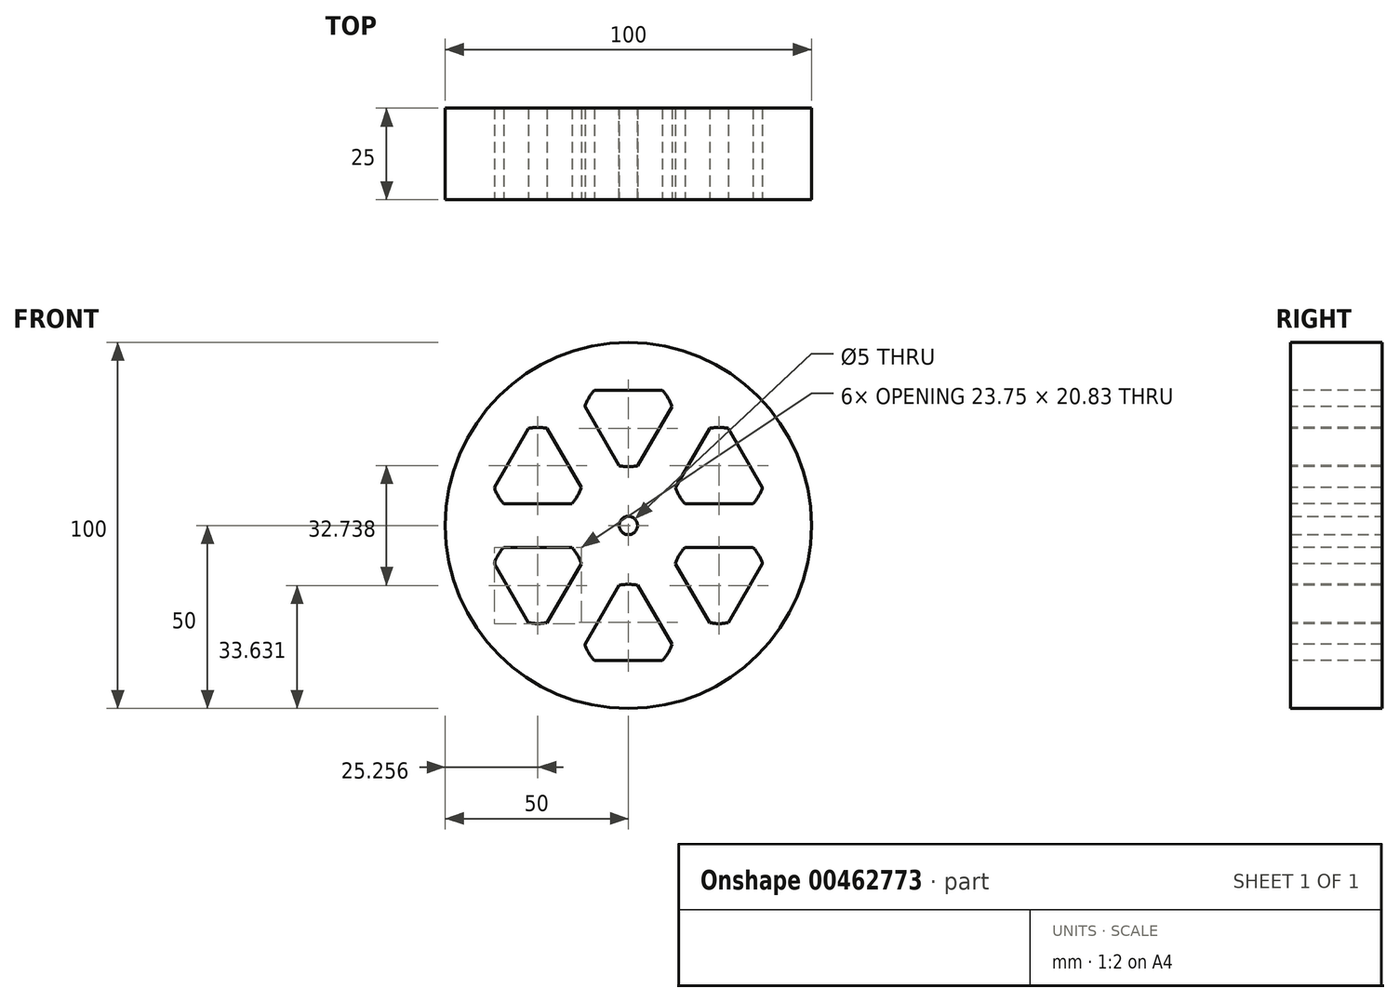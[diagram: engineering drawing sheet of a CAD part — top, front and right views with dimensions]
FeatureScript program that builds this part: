
annotation { "Feature Type Name" : "Feature", "Feature Type Description" : "" }
export const myFeature = defineFeature(function(context is Context, id is Id, definition is map)
    precondition{}
    {
        {
            var Q0;
            Q0=qCreatedBy(makeId("Front.planeOp"),FACE);
            var sketch = newSketch(context, id + "F0", { "sketchPlane" : qUnion([Q0])});
            skCircle(sketch, "E0", {"center": v(0, 0) * mm, "radius": 50 * mm});
            skCircle(sketch, "E1", {"center": v(0, 0) * mm, "radius": 2.5 * mm});
            skSolve(sketch);
        }
        {
            var Q0;
            Q0=qSketchRegion(id+"F0",true);
            extrude(context, id + "F1", {"entities" : qUnion([Q0]), "depth" : 25 * mm});
        }
        {
            var Q0;
            Q0=makeQuery(id+"F1.opExtrude","CAP_FACE",FACE,{"disambiguationData":[OSD([sQuery(id+"F0.wireOp",EDGE,"E0"),sQuery(id+"F0.wireOp",EDGE,"E1")])],"isStart":false});
            var sketch = newSketch(context, id + "F2", { "sketchPlane" : qUnion([Q0])});
            skCircle(sketch, "E2.cCircle", {"center": v(0, 28.57) * mm, "radius": 8.33 * mm, "construction": true});
            skLineSegment(sketch, "E2.0", {"start": v(14.43, 36.9) * mm, "end": v(0, 11.9) * mm});
            skLineSegment(sketch, "E2.1", {"start": v(0, 11.9) * mm, "end": v(-14.43, 36.9) * mm});
            skLineSegment(sketch, "E2.2", {"start": v(-14.43, 36.9) * mm, "end": v(14.43, 36.9) * mm});
            skPoint(sketch, "E2.0.midPoint", {"position": v(7.22, 24.4) * mm});
            skLineSegment(sketch, "E3", {"start": v(0, 0) * mm, "end": v(77.64, 0) * mm, "construction": true});
            skPoint(sketch, "E4.center", {"position": v(0, 0) * mm});
            skLineSegment(sketch, "E5", {"start": v(0, 0) * mm, "end": v(0, 56.69) * mm, "construction": true});
            skCircle(sketch, "E6.cCircle", {"center": v(24.74, 14.29) * mm, "radius": 8.33 * mm, "construction": true});
            skLineSegment(sketch, "E6.0", {"start": v(24.74, 30.95) * mm, "end": v(39.18, 5.95) * mm});
            skLineSegment(sketch, "E6.1", {"start": v(39.18, 5.95) * mm, "end": v(10.3, 5.95) * mm});
            skLineSegment(sketch, "E6.2", {"start": v(10.3, 5.95) * mm, "end": v(24.74, 30.95) * mm});
            skPoint(sketch, "E6.0.midPoint", {"position": v(31.96, 18.45) * mm});
            skLineSegment(sketch, "E7", {"start": v(10.3, 5.95) * mm, "end": v(36.54, 21.1) * mm, "construction": true});
            skLineSegment(sketch, "E8.1.0", {"start": v(-39.18, 5.95) * mm, "end": v(-24.74, 30.95) * mm});
            skLineSegment(sketch, "E8.1.1", {"start": v(-10.3, 5.95) * mm, "end": v(-39.18, 5.95) * mm});
            skLineSegment(sketch, "E8.1.2", {"start": v(-24.74, 30.95) * mm, "end": v(-10.3, 5.95) * mm});
            skLineSegment(sketch, "E8.1.3", {"start": v(-10.3, -5.95) * mm, "end": v(-24.74, -30.95) * mm});
            skLineSegment(sketch, "E8.1.4", {"start": v(-24.74, -30.95) * mm, "end": v(-39.18, -5.95) * mm});
            skLineSegment(sketch, "E8.1.5", {"start": v(-39.18, -5.95) * mm, "end": v(-10.3, -5.95) * mm});
            skLineSegment(sketch, "E8.2.0", {"start": v(14.43, -36.9) * mm, "end": v(-14.43, -36.9) * mm});
            skLineSegment(sketch, "E8.2.1", {"start": v(0, -11.9) * mm, "end": v(14.43, -36.9) * mm});
            skLineSegment(sketch, "E8.2.2", {"start": v(-14.43, -36.9) * mm, "end": v(0, -11.9) * mm});
            skLineSegment(sketch, "E8.2.3", {"start": v(10.3, -5.95) * mm, "end": v(39.18, -5.95) * mm});
            skLineSegment(sketch, "E8.2.4", {"start": v(39.18, -5.95) * mm, "end": v(24.74, -30.95) * mm});
            skLineSegment(sketch, "E8.2.5", {"start": v(24.74, -30.95) * mm, "end": v(10.3, -5.95) * mm});
            skCircle(sketch, "E9", {"center": v(0, 28.57) * mm, "radius": 12.5 * mm});
            skCircle(sketch, "E10", {"center": v(24.74, 14.29) * mm, "radius": 12.5 * mm});
            skCircle(sketch, "E11.1.0", {"center": v(-24.74, -14.29) * mm, "radius": 12.5 * mm});
            skCircle(sketch, "E11.1.1", {"center": v(-24.74, 14.29) * mm, "radius": 12.5 * mm});
            skCircle(sketch, "E11.2.0", {"center": v(24.74, -14.29) * mm, "radius": 12.5 * mm});
            skCircle(sketch, "E11.2.1", {"center": v(0, -28.57) * mm, "radius": 12.5 * mm});
            skSolve(sketch);
        }
        {
            var Q0;
            {var subQ0=sQuery(id+"F2.wireOp",EDGE,"E9");var subQ4=sQuery(id+"F2.wireOp",EDGE,"E2.0");var subQ5=makeQuery(id+"F2.imprint","INTERSECT",VERTEX,{"disambiguationData":[OD(0.0)],"derivedFrom":[subQ4,subQ0]});Q0=makeQuery(id+"F2.imprint","IMPRINT",FACE,{"disambiguationData":[TD([[makeQuery(id+"F2.imprint","IMPRINT",EDGE,{"disambiguationData":[TD([[subQ5,-1.0]])],"derivedFrom":subQ4}),-1.0]])]});}
            var Q1;
            {var subQ0=sQuery(id+"F2.wireOp",EDGE,"E10");var subQ4=sQuery(id+"F2.wireOp",EDGE,"E6.0");var subQ5=makeQuery(id+"F2.imprint","INTERSECT",VERTEX,{"disambiguationData":[OD(0.0)],"derivedFrom":[subQ4,subQ0]});Q1=makeQuery(id+"F2.imprint","IMPRINT",FACE,{"disambiguationData":[TD([[makeQuery(id+"F2.imprint","IMPRINT",EDGE,{"disambiguationData":[TD([[subQ5,-1.0]])],"derivedFrom":subQ4}),-1.0]])]});}
            var Q2;
            {var subQ0=sQuery(id+"F2.wireOp",EDGE,"E11.1.1");var subQ4=sQuery(id+"F2.wireOp",EDGE,"E8.1.0");var subQ5=makeQuery(id+"F2.imprint","INTERSECT",VERTEX,{"disambiguationData":[OD(0.0)],"derivedFrom":[subQ4,subQ0]});Q2=makeQuery(id+"F2.imprint","IMPRINT",FACE,{"disambiguationData":[TD([[makeQuery(id+"F2.imprint","IMPRINT",EDGE,{"disambiguationData":[TD([[subQ5,-1.0]])],"derivedFrom":subQ4}),-1.0]])]});}
            var Q3;
            {var subQ0=sQuery(id+"F2.wireOp",EDGE,"E11.1.0");var subQ7=sQuery(id+"F2.wireOp",EDGE,"E8.1.3");var subQ8=makeQuery(id+"F2.imprint","INTERSECT",VERTEX,{"disambiguationData":[OD(0.0)],"derivedFrom":[subQ7,subQ0]});Q3=makeQuery(id+"F2.imprint","IMPRINT",FACE,{"disambiguationData":[TD([[makeQuery(id+"F2.imprint","IMPRINT",EDGE,{"disambiguationData":[TD([[subQ8,-1.0]])],"derivedFrom":subQ7}),-1.0]])]});}
            var Q4;
            {var subQ0=sQuery(id+"F2.wireOp",EDGE,"E11.2.1");var subQ1=sQuery(id+"F2.wireOp",EDGE,"E8.2.0");var subQ2=makeQuery(id+"F2.imprint","INTERSECT",VERTEX,{"disambiguationData":[OD(0.0)],"derivedFrom":[subQ1,subQ0]});Q4=makeQuery(id+"F2.imprint","IMPRINT",FACE,{"disambiguationData":[TD([[makeQuery(id+"F2.imprint","IMPRINT",EDGE,{"disambiguationData":[TD([[subQ2,-1.0]])],"derivedFrom":subQ1}),-1.0]])]});}
            var Q5;
            {var subQ0=sQuery(id+"F2.wireOp",EDGE,"E11.2.0");var subQ7=sQuery(id+"F2.wireOp",EDGE,"E8.2.3");var subQ8=makeQuery(id+"F2.imprint","INTERSECT",VERTEX,{"disambiguationData":[OD(0.0)],"derivedFrom":[subQ7,subQ0]});Q5=makeQuery(id+"F2.imprint","IMPRINT",FACE,{"disambiguationData":[TD([[makeQuery(id+"F2.imprint","IMPRINT",EDGE,{"disambiguationData":[TD([[subQ8,-1.0]])],"derivedFrom":subQ7}),-1.0]])]});}
            extrude(context, id + "F3", {"entities" : qUnion([Q0, Q1, Q2, Q3, Q4, Q5]), "operationType" : NewBodyOperationType.REMOVE, "oppositeDirection" : true, "depth" : 25 * mm});
        }
    });
